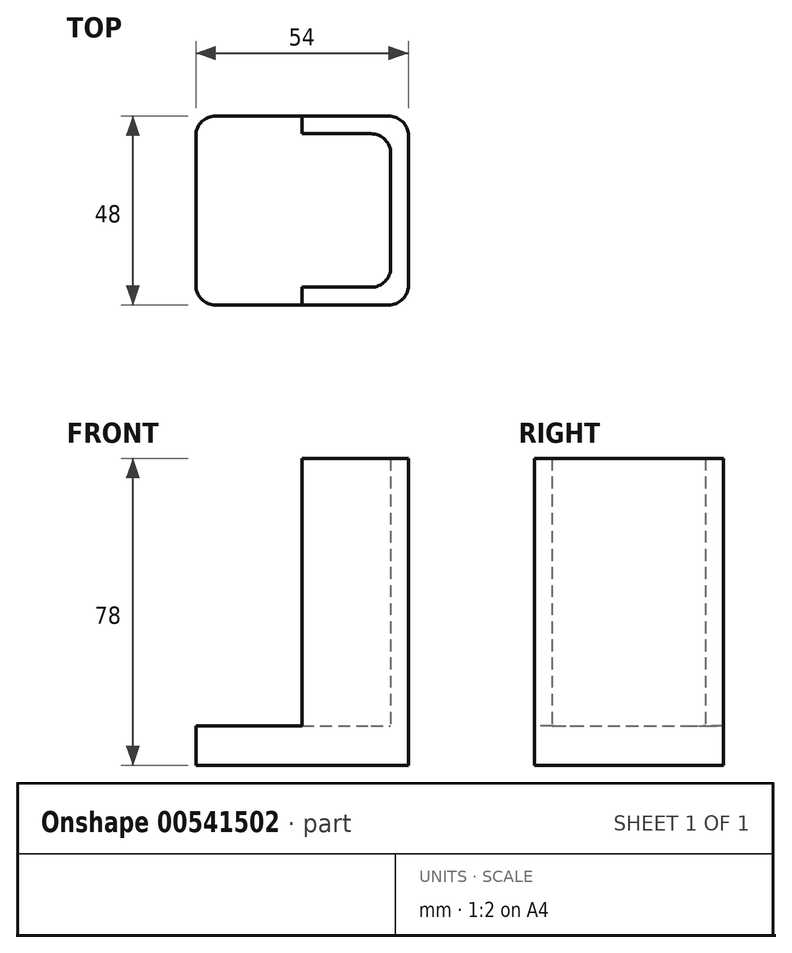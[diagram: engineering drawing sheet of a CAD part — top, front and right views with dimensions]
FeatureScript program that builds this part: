
annotation { "Feature Type Name" : "Feature", "Feature Type Description" : "" }
export const myFeature = defineFeature(function(context is Context, id is Id, definition is map)
    precondition{}
    {
        {
            var Q0;
            Q0=qCreatedBy(makeId("Top.planeOp"),FACE);
            var sketch = newSketch(context, id + "F0", { "sketchPlane" : qUnion([Q0])});
            skLineSegment(sketch, "E0.bottom", {"start": v(5, 0) * mm, "end": v(40, 0) * mm});
            skLineSegment(sketch, "E0.top", {"start": v(5, 39) * mm, "end": v(40, 39) * mm});
            skLineSegment(sketch, "E0.left", {"start": v(0, 5) * mm, "end": v(0, 34) * mm});
            skLineSegment(sketch, "E0.right", {"start": v(45, 5) * mm, "end": v(45, 34) * mm});
            skLineSegment(sketch, "E1.bottom", {"start": v(0.5, -4.5) * mm, "end": v(44.5, -4.5) * mm});
            skLineSegment(sketch, "E1.top", {"start": v(0.5, 43.5) * mm, "end": v(44.5, 43.5) * mm});
            skLineSegment(sketch, "E1.left", {"start": v(-4.5, 0.5) * mm, "end": v(-4.5, 38.5) * mm});
            skLineSegment(sketch, "E1.right", {"start": v(49.5, 0.5) * mm, "end": v(49.5, 38.5) * mm});
            skPoint(sketch, "E2.visualSharp", {"position": v(45, 0) * mm});
            skArc(sketch, "E2.filletArc", {"start": v(40, 0) * mm, "mid": v(43.54, 1.46) * mm, "end": v(45, 5) * mm});
            skPoint(sketch, "E3.visualSharp", {"position": v(45, 39) * mm});
            skArc(sketch, "E3.filletArc", {"start": v(45, 34) * mm, "mid": v(43.54, 37.54) * mm, "end": v(40, 39) * mm});
            skPoint(sketch, "E4.visualSharp", {"position": v(0, 39) * mm});
            skArc(sketch, "E4.filletArc", {"start": v(5, 39) * mm, "mid": v(1.46, 37.54) * mm, "end": v(0, 34) * mm});
            skPoint(sketch, "E5.visualSharp", {"position": v(49.5, -4.5) * mm});
            skArc(sketch, "E5.filletArc", {"start": v(44.5, -4.5) * mm, "mid": v(48.04, -3.04) * mm, "end": v(49.5, 0.5) * mm});
            skPoint(sketch, "E6.visualSharp", {"position": v(49.5, 43.5) * mm});
            skArc(sketch, "E6.filletArc", {"start": v(49.5, 38.5) * mm, "mid": v(48.04, 42.04) * mm, "end": v(44.5, 43.5) * mm});
            skPoint(sketch, "E7.visualSharp", {"position": v(-4.5, 43.5) * mm});
            skArc(sketch, "E7.filletArc", {"start": v(0.5, 43.5) * mm, "mid": v(-3.04, 42.04) * mm, "end": v(-4.5, 38.5) * mm});
            skPoint(sketch, "E8.visualSharp", {"position": v(0, 0) * mm});
            skArc(sketch, "E8.filletArc", {"start": v(0, 5) * mm, "mid": v(1.46, 1.46) * mm, "end": v(5, 0) * mm});
            skPoint(sketch, "E9.visualSharp", {"position": v(-4.5, -4.5) * mm});
            skArc(sketch, "E9.filletArc", {"start": v(-4.5, 0.5) * mm, "mid": v(-3.04, -3.04) * mm, "end": v(0.5, -4.5) * mm});
            skLineSegment(sketch, "E10", {"start": v(22.5, 0) * mm, "end": v(22.5, -4.5) * mm});
            skLineSegment(sketch, "E11", {"start": v(22.5, 39) * mm, "end": v(22.5, 43.5) * mm});
            skSolve(sketch);
        }
        {
            var Q0;
            Q0=makeQuery(id+"F0.imprint","IMPRINT",FACE,{"disambiguationData":[TD([[makeQuery(id+"F0.imprint","IMPRINT",EDGE,{"derivedFrom":sQuery(id+"F0.wireOp",EDGE,"E0.bottom")}),-1.0]])]});
            var Q1;
            Q1=makeQuery(id+"F0.imprint","IMPRINT",FACE,{"disambiguationData":[TD([[makeQuery(id+"F0.imprint","IMPRINT",EDGE,{"derivedFrom":sQuery(id+"F0.wireOp",EDGE,"E0.bottom")}),1.0]])]});
            extrude(context, id + "F1", {"entities" : qUnion([Q0, Q1]), "oppositeDirection" : true, "depth" : 10 * mm, "offsetDistance" : 25 * mm});
        }
        {
            var Q0;
            Q0=makeQuery(id+"F0.imprint","IMPRINT",FACE,{"disambiguationData":[TD([[makeQuery(id+"F0.imprint","IMPRINT",EDGE,{"derivedFrom":sQuery(id+"F0.wireOp",EDGE,"E0.right")}),-1.0]])]});
            extrude(context, id + "F2", {"entities" : qUnion([Q0]), "operationType" : NewBodyOperationType.ADD, "depth" : 68 * mm, "offsetDistance" : 25 * mm});
        }
        {
            var Q0;
            Q0=qCreatedBy(makeId("Top.planeOp"),FACE);
            cPlane(context, id + "F3", {"entities" : qUnion([Q0]), "cplaneType" : CPlaneType.OFFSET, "offset" : 20 * mm, "width" : 150 * mm, "height" : 150 * mm});
        }
    });
